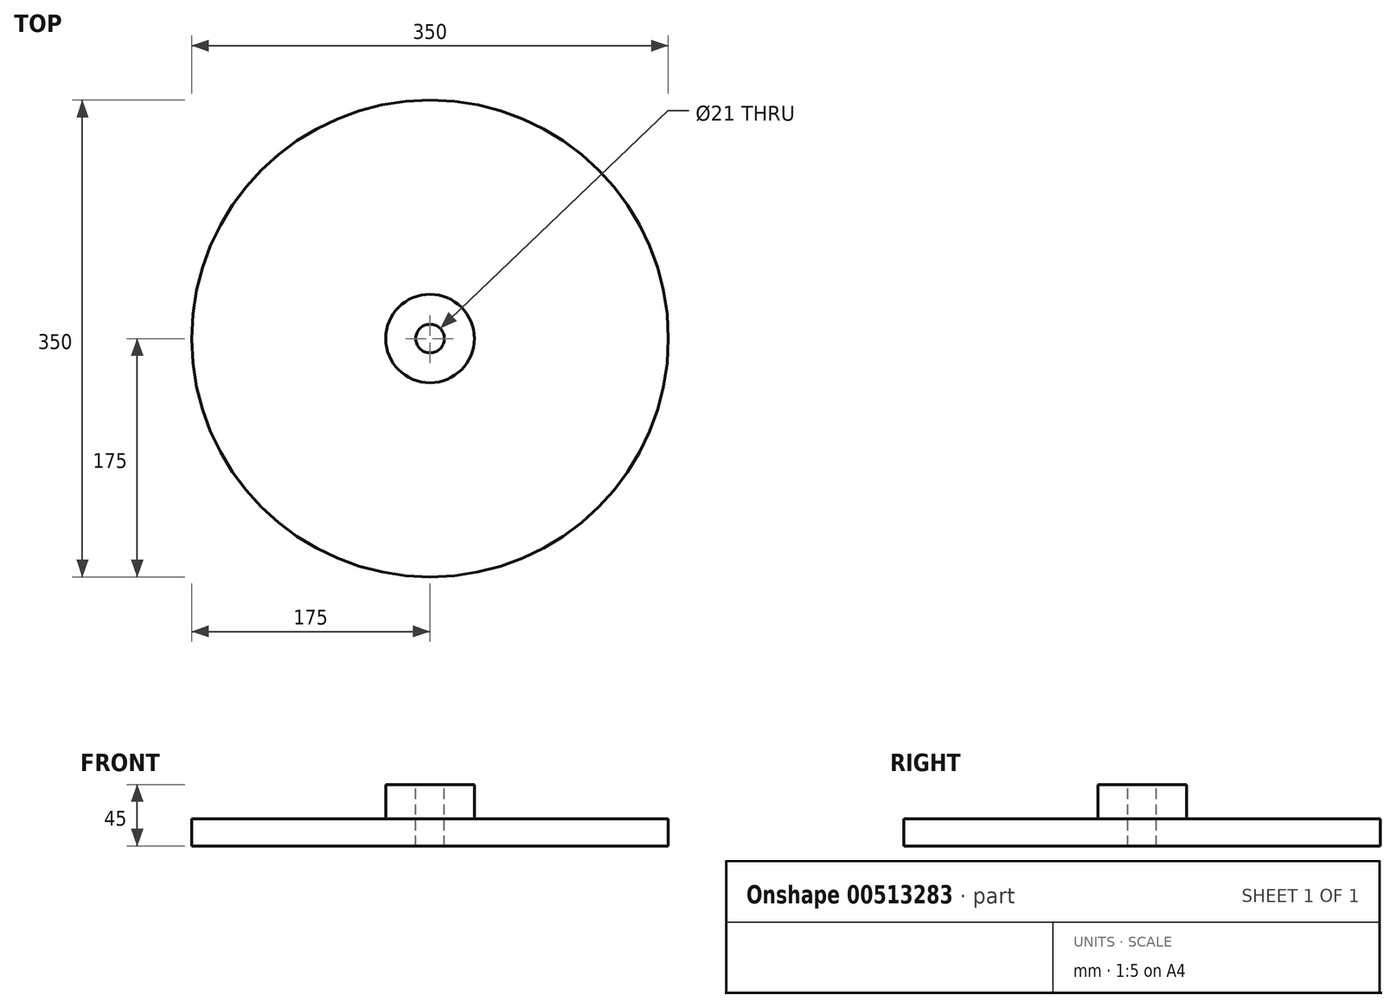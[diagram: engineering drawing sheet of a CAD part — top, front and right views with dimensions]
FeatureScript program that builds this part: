
annotation { "Feature Type Name" : "Feature", "Feature Type Description" : "" }
export const myFeature = defineFeature(function(context is Context, id is Id, definition is map)
    precondition{}
    {
        {
            var Q0;
            Q0=qCreatedBy(makeId("Top.planeOp"),FACE);
            var sketch = newSketch(context, id + "F0", { "sketchPlane" : qUnion([Q0])});
            skCircle(sketch, "E0", {"center": v(0, 0) * mm, "radius": 175 * mm});
            skCircle(sketch, "E1", {"center": v(0, 0) * mm, "radius": 32.5 * mm});
            skCircle(sketch, "E2", {"center": v(0, 0) * mm, "radius": 10.5 * mm});
            skSolve(sketch);
        }
        {
            var Q0;
            Q0=makeQuery(id+"F0.imprint","IMPRINT",FACE,{"disambiguationData":[TD([[makeQuery(id+"F0.imprint","IMPRINT",EDGE,{"derivedFrom":sQuery(id+"F0.wireOp",EDGE,"E0")}),1.0]])]});
            var Q1;
            Q1=makeQuery(id+"F0.imprint","IMPRINT",FACE,{"disambiguationData":[TD([[makeQuery(id+"F0.imprint","IMPRINT",EDGE,{"derivedFrom":sQuery(id+"F0.wireOp",EDGE,"E1")}),1.0]])]});
            extrude(context, id + "F1", {"entities" : qUnion([Q0, Q1]), "oppositeDirection" : true, "depth" : 20 * mm});
        }
        {
            var Q0;
            Q0=makeQuery(id+"F0.imprint","IMPRINT",FACE,{"disambiguationData":[TD([[makeQuery(id+"F0.imprint","IMPRINT",EDGE,{"derivedFrom":sQuery(id+"F0.wireOp",EDGE,"E1")}),1.0]])]});
            extrude(context, id + "F2", {"entities" : qUnion([Q0]), "operationType" : NewBodyOperationType.ADD, "depth" : 25 * mm});
        }
    });
